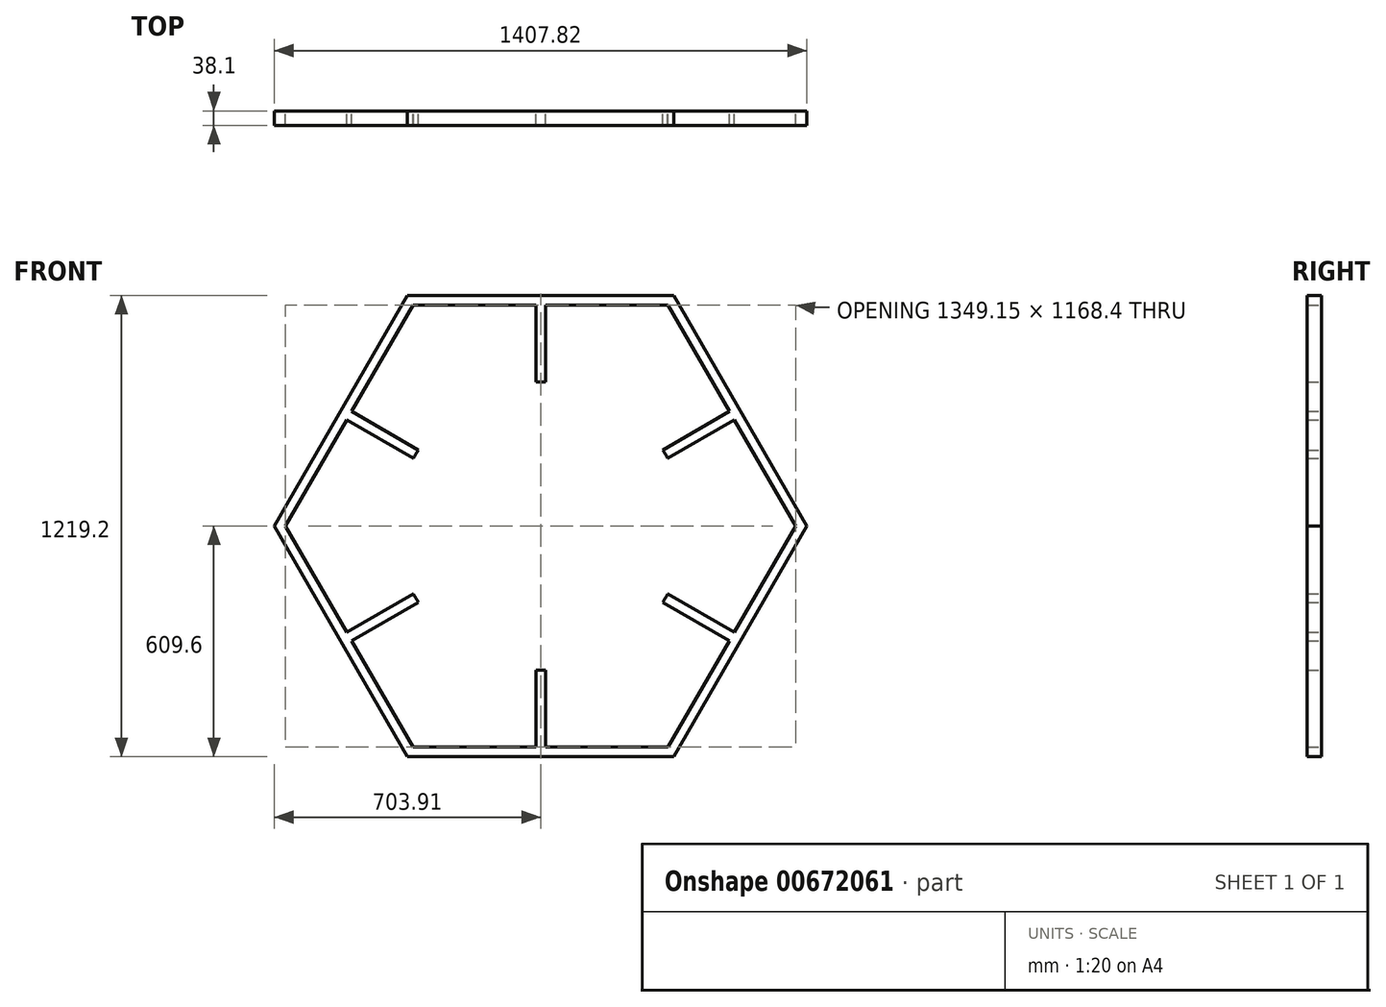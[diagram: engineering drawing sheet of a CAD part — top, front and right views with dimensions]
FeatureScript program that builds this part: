
annotation { "Feature Type Name" : "Feature", "Feature Type Description" : "" }
export const myFeature = defineFeature(function(context is Context, id is Id, definition is map)
    precondition{}
    {
        {
            var Q0;
            Q0=qCreatedBy(makeId("Front.planeOp"),FACE);
            var sketch = newSketch(context, id + "F0", { "sketchPlane" : qUnion([Q0])});
            skCircle(sketch, "E0.cCircle", {"center": v(0, 0) * mm, "radius": 584.2 * mm, "construction": true});
            skLineSegment(sketch, "E0.0", {"start": v(337.29, 584.2) * mm, "end": v(674.58, 0) * mm});
            skLineSegment(sketch, "E0.1", {"start": v(674.58, 0) * mm, "end": v(337.29, -584.2) * mm});
            skLineSegment(sketch, "E0.2", {"start": v(337.29, -584.2) * mm, "end": v(-337.29, -584.2) * mm});
            skLineSegment(sketch, "E0.3", {"start": v(-337.29, -584.2) * mm, "end": v(-674.58, 0) * mm});
            skLineSegment(sketch, "E0.4", {"start": v(-674.58, 0) * mm, "end": v(-499.58, 303.1) * mm});
            skLineSegment(sketch, "E0.5", {"start": v(-337.29, 584.2) * mm, "end": v(337.29, 584.2) * mm});
            skPoint(sketch, "E0.0.midPoint", {"position": v(505.93, 292.1) * mm});
            skCircle(sketch, "E1", {"center": v(0, 0) * mm, "radius": 381 * mm});
            skLineSegment(sketch, "E2", {"start": v(-512.28, 281.1) * mm, "end": v(-336.12, 179.4) * mm});
            skLineSegment(sketch, "E3", {"start": v(-499.58, 303.1) * mm, "end": v(-323.42, 201.4) * mm});
            skLineSegment(sketch, "E4", {"start": v(-337.29, 584.2) * mm, "end": v(-337.29, 584.2) * mm});
            skLineSegment(sketch, "E5", {"start": v(-512.28, 281.1) * mm, "end": v(-337.29, 584.2) * mm});
            skLineSegment(sketch, "E6", {"start": v(-499.58, 303.1) * mm, "end": v(-449.94, 389.08) * mm});
            skLineSegment(sketch, "E7", {"start": v(-674.58, 0) * mm, "end": v(-674.58, 0) * mm});
            skPoint(sketch, "E8.center", {"position": v(38, -49.16) * mm});
            skLineSegment(sketch, "E9", {"start": v(-1099.5, 381) * mm, "end": v(1284.02, 381) * mm, "construction": true});
            skLineSegment(sketch, "E10", {"start": v(-1101.82, -381) * mm, "end": v(1466.6, -381) * mm, "construction": true});
            skLineSegment(sketch, "E11.1.0", {"start": v(-499.58, -303.1) * mm, "end": v(-323.42, -201.4) * mm});
            skLineSegment(sketch, "E11.1.1", {"start": v(-512.28, -281.1) * mm, "end": v(-336.12, -179.4) * mm});
            skLineSegment(sketch, "E11.2.0", {"start": v(12.7, -584.2) * mm, "end": v(12.7, -380.79) * mm});
            skLineSegment(sketch, "E11.2.1", {"start": v(-12.7, -584.2) * mm, "end": v(-12.7, -380.79) * mm});
            skLineSegment(sketch, "E11.3.0", {"start": v(512.28, -281.1) * mm, "end": v(336.12, -179.4) * mm});
            skLineSegment(sketch, "E11.3.1", {"start": v(499.58, -303.1) * mm, "end": v(323.42, -201.4) * mm});
            skLineSegment(sketch, "E11.4.0", {"start": v(499.58, 303.1) * mm, "end": v(323.42, 201.4) * mm});
            skLineSegment(sketch, "E11.4.1", {"start": v(512.28, 281.1) * mm, "end": v(336.12, 179.4) * mm});
            skLineSegment(sketch, "E11.5.0", {"start": v(-12.7, 584.2) * mm, "end": v(-12.7, 380.79) * mm});
            skLineSegment(sketch, "E11.5.1", {"start": v(12.7, 584.2) * mm, "end": v(12.7, 380.79) * mm});
            skCircle(sketch, "E12.cCircle", {"center": v(0, 0) * mm, "radius": 609.6 * mm, "construction": true});
            skLineSegment(sketch, "E12.0", {"start": v(-351.95, 609.6) * mm, "end": v(351.95, 609.6) * mm});
            skLineSegment(sketch, "E12.1", {"start": v(351.95, 609.6) * mm, "end": v(703.9, 0) * mm});
            skLineSegment(sketch, "E12.2", {"start": v(703.9, 0) * mm, "end": v(351.95, -609.6) * mm});
            skLineSegment(sketch, "E12.3", {"start": v(351.95, -609.6) * mm, "end": v(-351.95, -609.6) * mm});
            skLineSegment(sketch, "E12.4", {"start": v(-351.95, -609.6) * mm, "end": v(-703.9, 0) * mm});
            skLineSegment(sketch, "E12.5", {"start": v(-703.9, 0) * mm, "end": v(-351.95, 609.6) * mm});
            skPoint(sketch, "E12.0.midPoint", {"position": v(0, 609.6) * mm});
            skSolve(sketch);
        }
        {
            var Q0;
            {var subQ0=sQuery(id+"F0.wireOp",EDGE,"E11.5.0");Q0=makeQuery(id+"F0.imprint","IMPRINT",FACE,{"disambiguationData":[TD([[makeQuery(id+"F0.imprint","IMPRINT",EDGE,{"derivedFrom":subQ0}),1.0]])]});}
            var Q1;
            {var subQ0=sQuery(id+"F0.wireOp",EDGE,"E2");Q1=makeQuery(id+"F0.imprint","IMPRINT",FACE,{"disambiguationData":[TD([[makeQuery(id+"F0.imprint","IMPRINT",EDGE,{"derivedFrom":subQ0}),1.0]])]});}
            var Q2;
            {var subQ0=sQuery(id+"F0.wireOp",EDGE,"E11.4.0");Q2=makeQuery(id+"F0.imprint","IMPRINT",FACE,{"disambiguationData":[TD([[makeQuery(id+"F0.imprint","IMPRINT",EDGE,{"derivedFrom":subQ0}),1.0]])]});}
            var Q3;
            {var subQ0=sQuery(id+"F0.wireOp",EDGE,"E11.3.0");Q3=makeQuery(id+"F0.imprint","IMPRINT",FACE,{"disambiguationData":[TD([[makeQuery(id+"F0.imprint","IMPRINT",EDGE,{"derivedFrom":subQ0}),1.0]])]});}
            var Q4;
            {var subQ0=sQuery(id+"F0.wireOp",EDGE,"E11.2.0");Q4=makeQuery(id+"F0.imprint","IMPRINT",FACE,{"disambiguationData":[TD([[makeQuery(id+"F0.imprint","IMPRINT",EDGE,{"derivedFrom":subQ0}),1.0]])]});}
            var Q5;
            {var subQ0=sQuery(id+"F0.wireOp",EDGE,"E11.1.0");Q5=makeQuery(id+"F0.imprint","IMPRINT",FACE,{"disambiguationData":[TD([[makeQuery(id+"F0.imprint","IMPRINT",EDGE,{"derivedFrom":subQ0}),1.0]])]});}
            var Q6;
            {var subQ6=sQuery(id+"F0.wireOp",EDGE,"E0.4");Q6=makeQuery(id+"F0.imprint","IMPRINT",FACE,{"disambiguationData":[TD([[makeQuery(id+"F0.imprint","IMPRINT",EDGE,{"derivedFrom":subQ6}),1.0]])]});}
            extrude(context, id + "F1", {"entities" : qUnion([Q0, Q1, Q2, Q3, Q4, Q5, Q6]), "depth" : 38.1 * mm, "offsetDistance" : 25.4 * mm});
        }
    });
